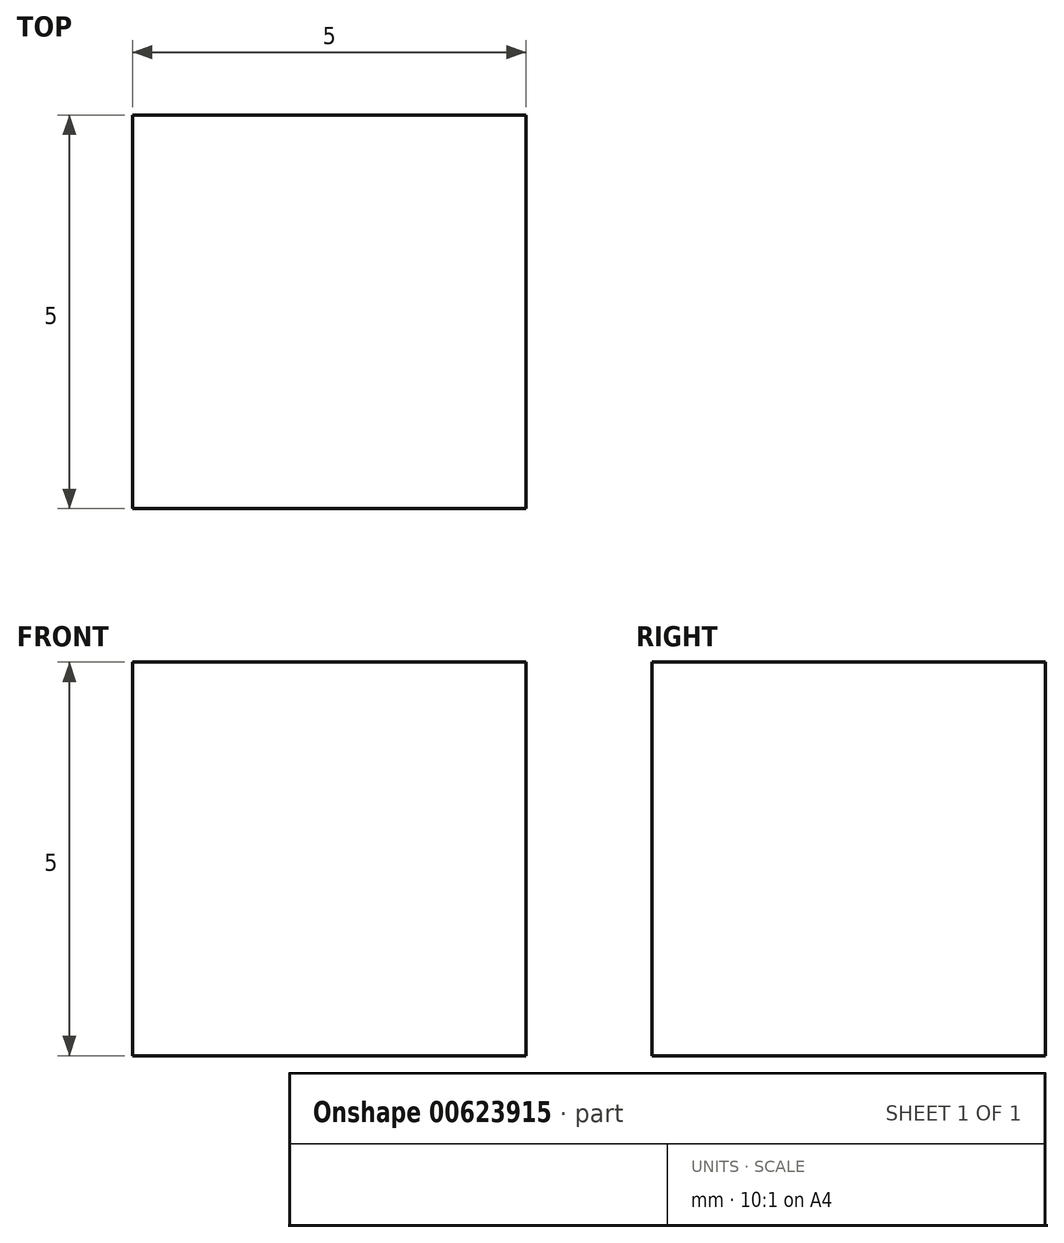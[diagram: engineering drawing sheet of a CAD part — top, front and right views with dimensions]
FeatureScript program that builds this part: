
annotation { "Feature Type Name" : "Feature", "Feature Type Description" : "" }
export const myFeature = defineFeature(function(context is Context, id is Id, definition is map)
    precondition{}
    {
        {
            var Q0;
            Q0=qCreatedBy(makeId("Top.planeOp"),FACE);
            var sketch = newSketch(context, id + "F0", { "sketchPlane" : qUnion([Q0])});
            skLineSegment(sketch, "E0.bottom", {"start": v(2.5, 2.5) * mm, "end": v(-2.5, 2.5) * mm});
            skLineSegment(sketch, "E0.top", {"start": v(2.5, -2.5) * mm, "end": v(-2.5, -2.5) * mm});
            skLineSegment(sketch, "E0.left", {"start": v(2.5, 2.5) * mm, "end": v(2.5, -2.5) * mm});
            skLineSegment(sketch, "E0.right", {"start": v(-2.5, 2.5) * mm, "end": v(-2.5, -2.5) * mm});
            skPoint(sketch, "E0.middle", {"position": v(0, 0) * mm});
            skSolve(sketch);
        }
        {
            var Q0;
            Q0 = qSketchRegion(id + "F0", true);
            extrude(context, id + "F1", {"entities" : qUnion([Q0]), "depth" : 5 * mm, "offsetDistance" : 25 * mm});
        }
    });
